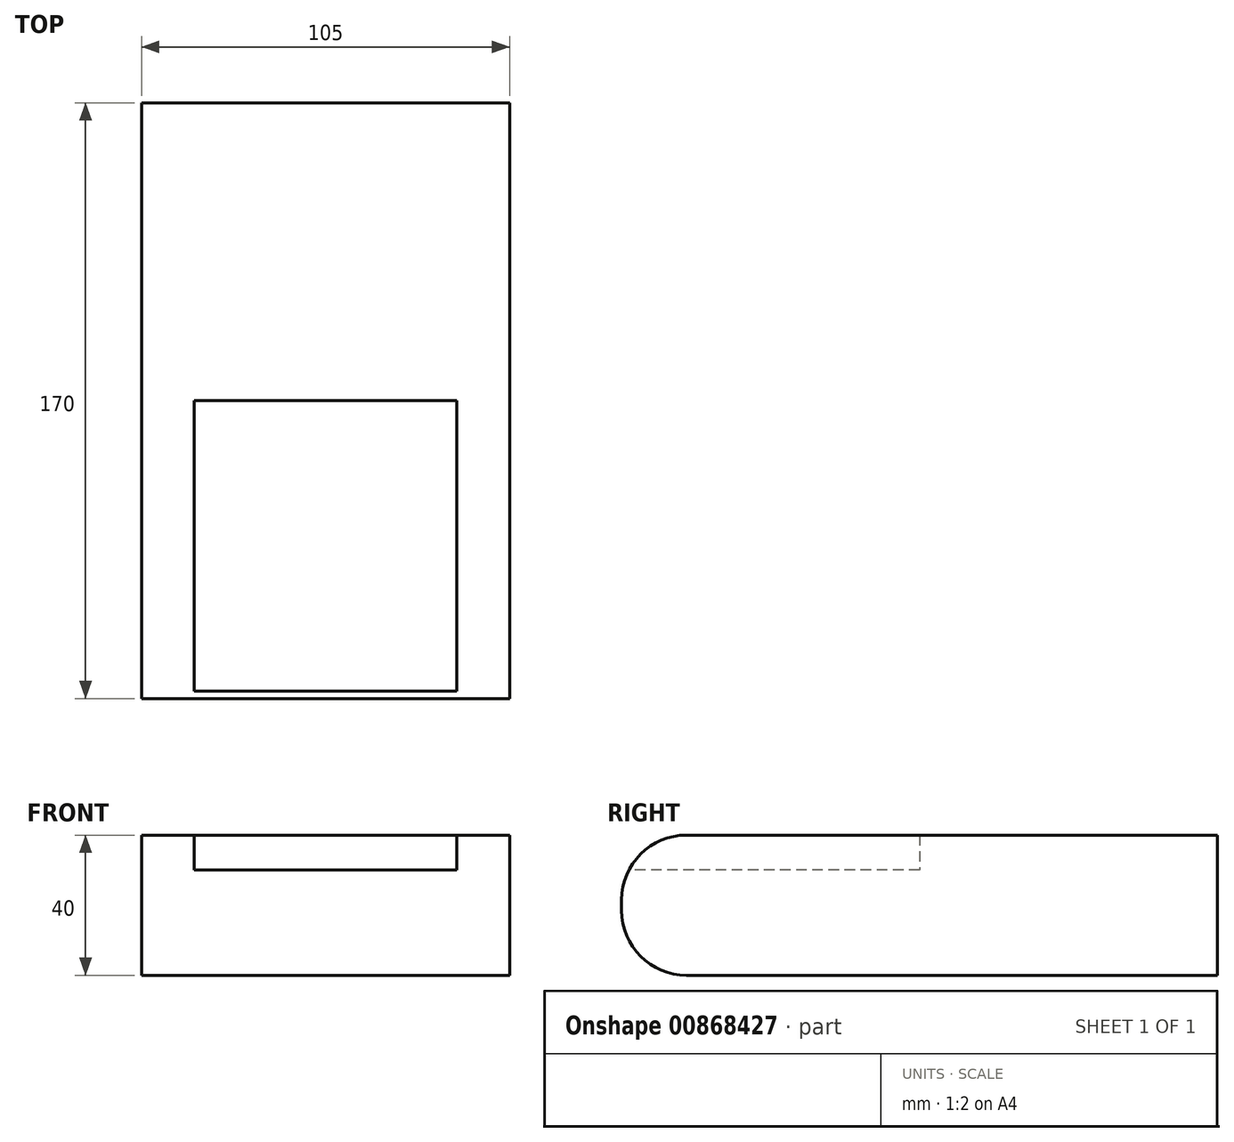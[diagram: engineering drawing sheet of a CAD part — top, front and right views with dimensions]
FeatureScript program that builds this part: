
annotation { "Feature Type Name" : "Feature", "Feature Type Description" : "" }
export const myFeature = defineFeature(function(context is Context, id is Id, definition is map)
    precondition{}
    {
        {
            var Q0;
            Q0=qCreatedBy(makeId("Right.planeOp"),FACE);
            var sketch = newSketch(context, id + "F0", { "sketchPlane" : qUnion([Q0])});
            skLineSegment(sketch, "E0.bottom", {"start": v(-85, 1.5) * mm, "end": v(85, 1.5) * mm});
            skLineSegment(sketch, "E0.top", {"start": v(-85, -1.5) * mm, "end": v(85, -1.5) * mm});
            skLineSegment(sketch, "E0.left", {"start": v(-85, 1.5) * mm, "end": v(-85, -1.5) * mm});
            skLineSegment(sketch, "E0.right", {"start": v(85, 1.5) * mm, "end": v(85, -1.5) * mm});
            skPoint(sketch, "E0.middle", {"position": v(0, 0) * mm});
            skLineSegment(sketch, "E1", {"start": v(-85, 1.5) * mm, "end": v(-85, 1.5) * mm});
            skLineSegment(sketch, "E2", {"start": v(-85, -1.5) * mm, "end": v(-85, -1.5) * mm});
            skPoint(sketch, "E3.visualSharp", {"position": v(-85, 25) * mm});
            skPoint(sketch, "E4.visualSharp", {"position": v(-85, -25) * mm});
            skLineSegment(sketch, "E5", {"start": v(85, 1.5) * mm, "end": v(85, 20) * mm});
            skLineSegment(sketch, "E6", {"start": v(85, 20) * mm, "end": v(-66.5, 20) * mm});
            skLineSegment(sketch, "E7", {"start": v(-66.5, -20) * mm, "end": v(85, -20) * mm});
            skLineSegment(sketch, "E8", {"start": v(85, -20) * mm, "end": v(85, -1.5) * mm});
            skPoint(sketch, "E9.visualSharp", {"position": v(-85, 20) * mm});
            skArc(sketch, "E9.filletArc", {"start": v(-66.5, 20) * mm, "mid": v(-79.58, 14.58) * mm, "end": v(-85, 1.5) * mm});
            skPoint(sketch, "E10.visualSharp", {"position": v(-85, -20) * mm});
            skArc(sketch, "E10.filletArc", {"start": v(-85, -1.5) * mm, "mid": v(-79.58, -14.58) * mm, "end": v(-66.5, -20) * mm});
            skSolve(sketch);
        }
        {
            var Q0;
            Q0=makeQuery(id+"F0.imprint","IMPRINT",FACE,{"disambiguationData":[TD([[makeQuery(id+"F0.imprint","IMPRINT",EDGE,{"derivedFrom":sQuery(id+"F0.wireOp",EDGE,"E0.bottom")}),1.0]])]});
            var Q1;
            Q1=makeQuery(id+"F0.imprint","IMPRINT",FACE,{"disambiguationData":[TD([[makeQuery(id+"F0.imprint","IMPRINT",EDGE,{"derivedFrom":sQuery(id+"F0.wireOp",EDGE,"E0.bottom")}),-1.0]])]});
            var Q2;
            Q2=makeQuery(id+"F0.imprint","IMPRINT",FACE,{"disambiguationData":[TD([[makeQuery(id+"F0.imprint","IMPRINT",EDGE,{"derivedFrom":sQuery(id+"F0.wireOp",EDGE,"E0.top")}),-1.0]])]});
            extrude(context, id + "F1", {"entities" : qUnion([Q0, Q1, Q2]), "endBound" : BoundingType.SYMMETRIC, "depth" : 105 * mm, "offsetDistance" : 25 * mm});
        }
        {
            var Q0;
            Q0=qCreatedBy(makeId("Right.planeOp"),FACE);
            var sketch = newSketch(context, id + "F2", { "sketchPlane" : qUnion([Q0])});
            skPoint(sketch, "E11.middle", {"position": v(0, 0) * mm});
            skLineSegment(sketch, "E12", {"start": v(0, 0) * mm, "end": v(85, 0) * mm});
            skLineSegment(sketch, "E13", {"start": v(85, 0) * mm, "end": v(75, 0) * mm});
            skLineSegment(sketch, "E14", {"start": v(75, 0) * mm, "end": v(75, 10) * mm});
            skLineSegment(sketch, "E15", {"start": v(75, 0) * mm, "end": v(75, -10) * mm});
            skLineSegment(sketch, "E16", {"start": v(75, -10) * mm, "end": v(75, -10) * mm});
            skLineSegment(sketch, "E17", {"start": v(75, -10) * mm, "end": v(25, -10) * mm});
            skLineSegment(sketch, "E18", {"start": v(25, -10) * mm, "end": v(25, 10) * mm});
            skLineSegment(sketch, "E19", {"start": v(25, 10) * mm, "end": v(75, 10) * mm});
            skLineSegment(sketch, "E20.bottom", {"start": v(-85, 20) * mm, "end": v(85, 20) * mm});
            skLineSegment(sketch, "E20.top", {"start": v(-85, -20) * mm, "end": v(85, -20) * mm});
            skLineSegment(sketch, "E20.left", {"start": v(-85, 20) * mm, "end": v(-85, -20) * mm});
            skLineSegment(sketch, "E20.right", {"start": v(85, 20) * mm, "end": v(85, -20) * mm});
            skLineSegment(sketch, "E21", {"start": v(0, 20) * mm, "end": v(0, 10) * mm});
            skLineSegment(sketch, "E22", {"start": v(0, 10) * mm, "end": v(-85, 10) * mm});
            skSolve(sketch);
        }
        {
            var Q0;
            {var subQ3=sQuery(id+"F2.wireOp",EDGE,"E21");Q0=makeQuery(id+"F2.imprint","IMPRINT",FACE,{"disambiguationData":[TD([[makeQuery(id+"F2.imprint","IMPRINT",EDGE,{"derivedFrom":subQ3}),-1.0]])]});}
            extrude(context, id + "F3", {"entities" : qUnion([Q0]), "operationType" : NewBodyOperationType.REMOVE, "endBound" : BoundingType.SYMMETRIC, "oppositeDirection" : true, "depth" : 75 * mm, "offsetDistance" : 25 * mm});
        }
    });
